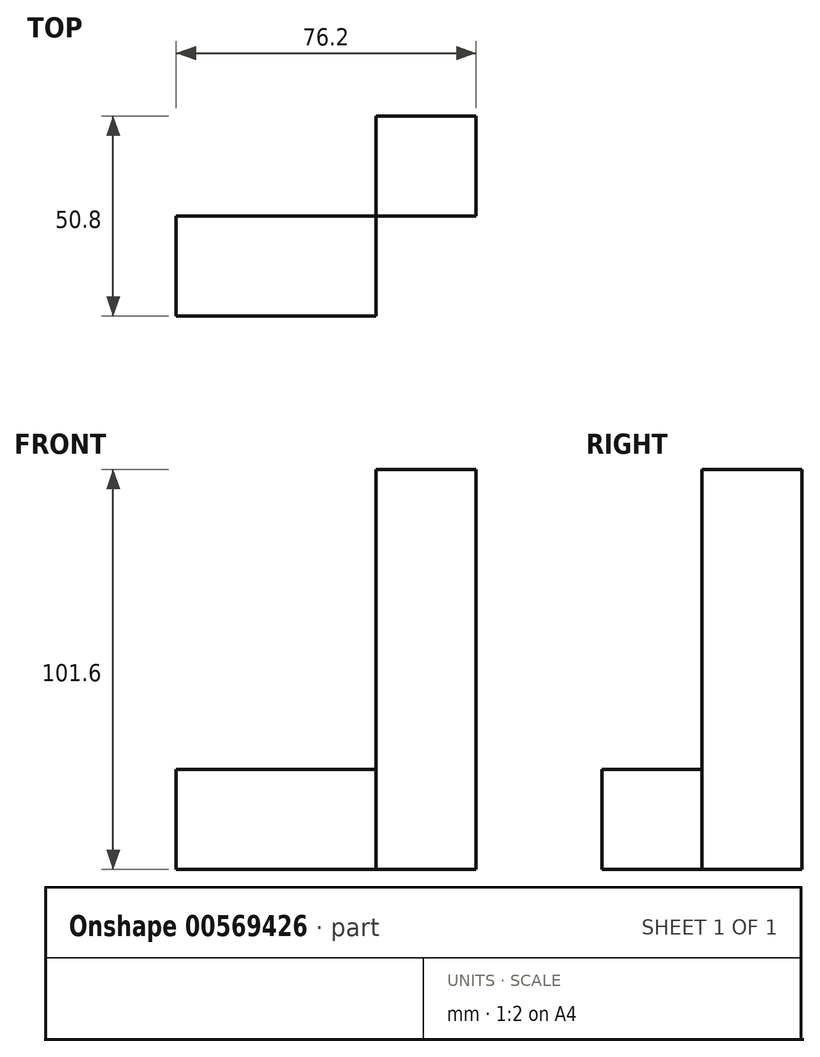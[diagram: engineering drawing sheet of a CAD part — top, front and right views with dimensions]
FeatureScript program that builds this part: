
annotation { "Feature Type Name" : "Feature", "Feature Type Description" : "" }
export const myFeature = defineFeature(function(context is Context, id is Id, definition is map)
    precondition{}
    {
        {
            var Q0;
            Q0=qCreatedBy(makeId("Front.planeOp"),FACE);
            var sketch = newSketch(context, id + "F0", { "sketchPlane" : qUnion([Q0])});
            skLineSegment(sketch, "E0.bottom", {"start": v(0, 0) * mm, "end": v(-50.8, 0) * mm});
            skLineSegment(sketch, "E0.top", {"start": v(0, 25.4) * mm, "end": v(-50.8, 25.4) * mm});
            skLineSegment(sketch, "E0.left", {"start": v(0, 0) * mm, "end": v(0, 25.4) * mm});
            skLineSegment(sketch, "E0.right", {"start": v(-50.8, 0) * mm, "end": v(-50.8, 25.4) * mm});
            skSolve(sketch);
        }
        {
            var Q0;
            Q0=makeQuery(id+"F0.imprint","IMPRINT",FACE,{"disambiguationData":[TD([[makeQuery(id+"F0.imprint","IMPRINT",EDGE,{"derivedFrom":sQuery(id+"F0.wireOp",EDGE,"E0.bottom")}),-1.0]])]});
            extrude(context, id + "F1", {"entities" : qUnion([Q0]), "depth" : 25.4 * mm, "offsetDistance" : 25.4 * mm});
        }
        {
            var Q0;
            Q0=qCreatedBy(makeId("Top.planeOp"),FACE);
            var sketch = newSketch(context, id + "F2", { "sketchPlane" : qUnion([Q0])});
            skLineSegment(sketch, "E1.bottom", {"start": v(0, 0) * mm, "end": v(25.4, 0) * mm});
            skLineSegment(sketch, "E1.top", {"start": v(0, 25.4) * mm, "end": v(25.4, 25.4) * mm});
            skLineSegment(sketch, "E1.left", {"start": v(0, 0) * mm, "end": v(0, 25.4) * mm});
            skLineSegment(sketch, "E1.right", {"start": v(25.4, 0) * mm, "end": v(25.4, 25.4) * mm});
            skSolve(sketch);
        }
        {
            var Q0;
            Q0=makeQuery(id+"F2.imprint","IMPRINT",FACE,{"disambiguationData":[TD([[makeQuery(id+"F2.imprint","IMPRINT",EDGE,{"derivedFrom":sQuery(id+"F2.wireOp",EDGE,"E1.bottom")}),1.0]])]});
            extrude(context, id + "F3", {"entities" : qUnion([Q0]), "depth" : 101.6 * mm, "offsetDistance" : 25.4 * mm});
        }
    });
